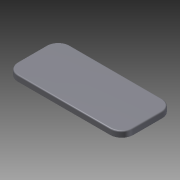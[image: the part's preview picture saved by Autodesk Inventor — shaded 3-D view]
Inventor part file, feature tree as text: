
AUTODESK INVENTOR PART (.ipt)
format: ipt  version: 2011 SP2 (Build 150309200, 309)  size: 96,256 bytes
history: native  units: mm
features: extrude x1, fillet x1, sketch x1
ambient origin geometry x8: Origin, YZ Plane, XZ Plane, XY Plane, X Axis, Y Axis, Z Axis, Center Point
bodies: Solid1 (feature_tree)
feature tree (3):
  extrude  "Extrusion1"  Depth=90.0mm
  fillet  "Fillet1"  Radius=45.0mm
  sketch  "Sketch1"  dims[d0=200.0mm d1=90.0mm d2=45.0mm d3=20.0mm d4=10.0mm d5=0.0mm d6=2.0mm]
